# Revit family: Scale-SR_Scales-SRV947IFS
name_source: partatom
category: Specialty Equipment
units: mm (PartAtom-declared; Revit-internal decimal feet)

## family parameters
Always vertical = Yes
Cut with Voids When Loaded = No
OmniClass Number = 23.40.70.11.14.11
OmniClass Title = Medical Equipment
Part Type = Normal
Room Calculation Point = No
Round Connector Dimension = Use Diameter
Shared = No
Work Plane-Based = No

## types (1)
- SRV947IFS
    Accuracy = 0.2% +/- 2 Digits of Displayed Resolution
    Assembly Code = E1020810
    Auto Power Down = Approximately 120 Seconds
    Averaging = Automatic Digital Filter
    BIM Version = v3.1
    BIM Version Available (Earliest) = 2017
    Calibration = Traceable to NIST Standards
    Default Elevation = 0"
    Description = 24" x 48" Portable (or Fixed) Platform Scale with Flush Wall Mounted Display
    Display Resolution = 0.2 lb / 0.1 kg
    Display Type = 1.0'' LCD Display with 5 Active Digits
    Manufacturer = SR Scales by SR Instruments, Inc.
    Maximum Weight Capacity = 400 lbs or 182 kg
    Model = SRV947IFS
    Platform Depth = 24"
    Platform Height Position = 0"
    Platform Size = "24'' x 48'' x 2" (61 cm x 122 cm x 5 cm)"
    Platform Width = 48"
    Power Supply = Six (6) AA 1.5 Volt Alkaline Batteries
    Product Brochure Link = https://srinstruments.com
    Product Page URL = https://srinstruments.com
    Show Flush Mounted Wall Display = Yes
    Show Recessed Pit Frame = Yes
    URL = http://www.srinstruments.com
    Zero = One Button Operation Auto Zero

## geometry (parser evidence)
native form markers: Blend x1, Sweep x5
no freeform markers — native parametric forms only
